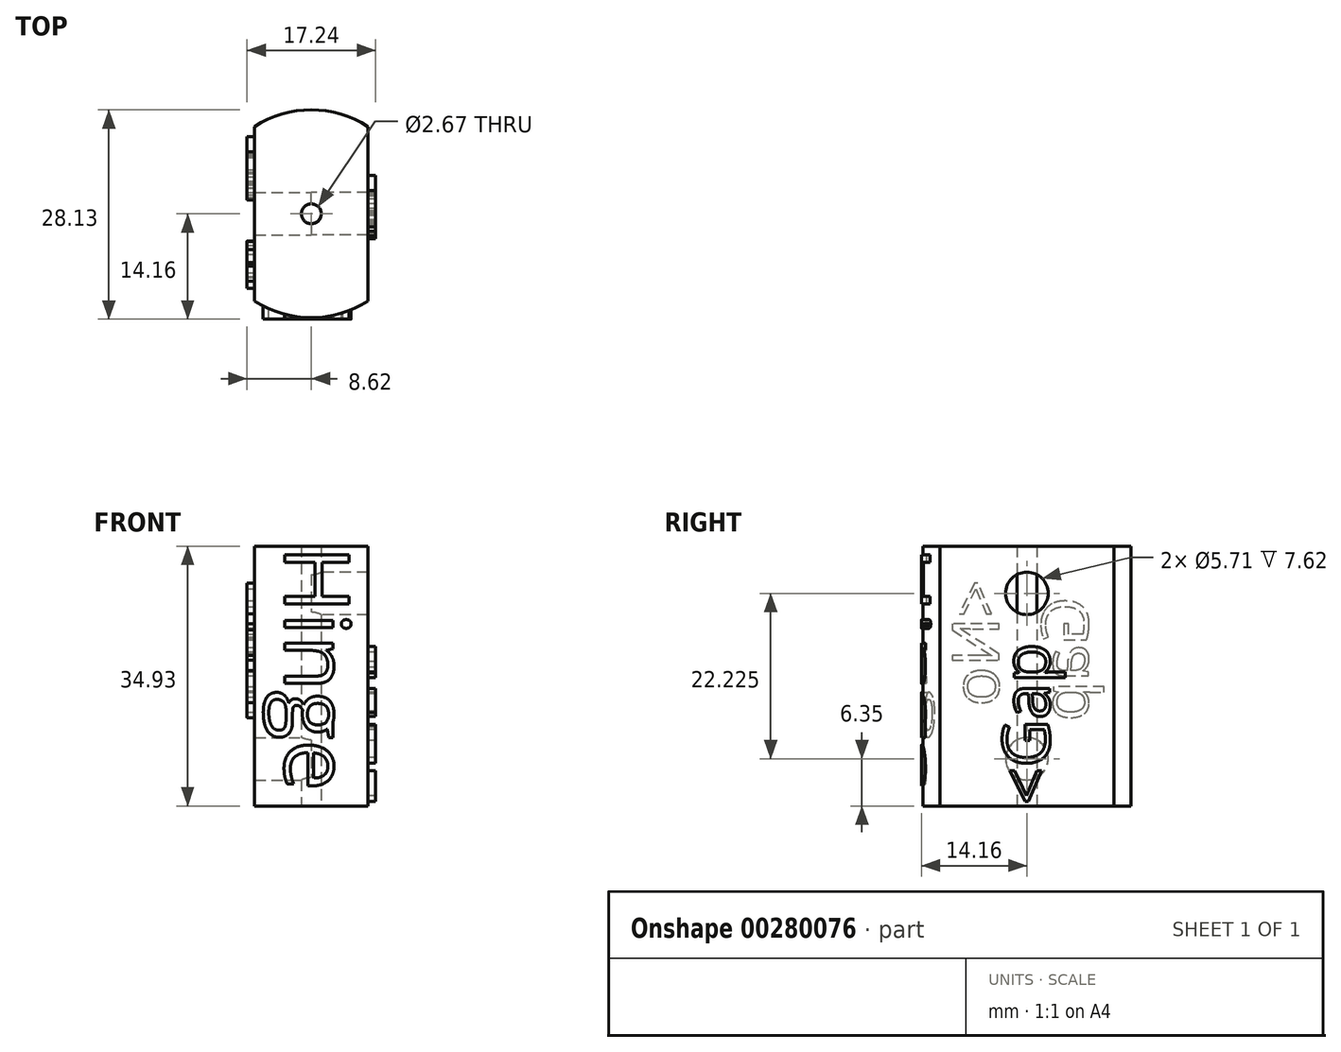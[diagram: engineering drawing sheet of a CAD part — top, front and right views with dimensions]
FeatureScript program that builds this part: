
annotation { "Feature Type Name" : "Feature", "Feature Type Description" : "" }
export const myFeature = defineFeature(function(context is Context, id is Id, definition is map)
    precondition{}
    {
        {
            var Q0;
            Q0=qCreatedBy(makeId("Top.planeOp"),FACE);
            var sketch = newSketch(context, id + "F0", { "sketchPlane" : qUnion([Q0])});
            skArc(sketch, "E0", {"start": v(-7.62, -11.7) * mm, "mid": v(0, -13.97) * mm, "end": v(7.62, -11.7) * mm});
            skCircle(sketch, "E1", {"center": v(0, 0) * mm, "radius": 1.33 * mm});
            skLineSegment(sketch, "E2", {"start": v(-7.62, -11.7) * mm, "end": v(-7.62, 11.7) * mm});
            skLineSegment(sketch, "E3.MirrorCS", {"start": v(7.62, -11.7) * mm, "end": v(7.62, 11.7) * mm});
            skArc(sketch, "E4.trimOffspring", {"start": v(7.62, 11.7) * mm, "mid": v(0, 13.97) * mm, "end": v(-7.62, 11.7) * mm});
            skSolve(sketch);
        }
        {
            var Q0;
            Q0=qSketchRegion(id+"F0",true);
            extrude(context, id + "F1", {"entities" : qUnion([Q0]), "depth" : 34.92 * mm});
        }
        {
            var Q0;
            Q0=qCreatedBy(makeId("Right.planeOp"),FACE);
            var sketch = newSketch(context, id + "F2", { "sketchPlane" : qUnion([Q0])});
            skCircle(sketch, "E5", {"center": v(0, 28.58) * mm, "radius": 2.86 * mm});
            skSolve(sketch);
        }
        {
            var Q0;
            Q0=qSketchRegion(id+"F2",true);
            var Q1;
            Q1=makeQuery(id+"F1.opExtrude","SWEPT_FACE",FACE,{"disambiguationData":[OSD([sQuery(id+"F0.wireOp",EDGE,"E3.MirrorCS")])]});
            extrude(context, id + "F3", {"entities" : qUnion([Q0]), "operationType" : NewBodyOperationType.REMOVE, "endBound" : BoundingType.UP_TO_SURFACE, "endBoundEntityFace" : qUnion([Q1]), "depth" : 6.35 * mm});
        }
        {
            var Q0;
            Q0=qCreatedBy(makeId("Right.planeOp"),FACE);
            var sketch = newSketch(context, id + "F4", { "sketchPlane" : qUnion([Q0])});
            skCircle(sketch, "E6", {"center": v(0, 6.35) * mm, "radius": 2.86 * mm});
            skSolve(sketch);
        }
        {
            var Q0;
            Q0=qSketchRegion(id+"F4",true);
            var Q1;
            Q1=makeQuery(id+"F1.opExtrude","SWEPT_FACE",FACE,{"disambiguationData":[OSD([sQuery(id+"F0.wireOp",EDGE,"E2")])]});
            extrude(context, id + "F5", {"entities" : qUnion([Q0]), "operationType" : NewBodyOperationType.REMOVE, "endBound" : BoundingType.UP_TO_SURFACE, "oppositeDirection" : true, "endBoundEntityFace" : qUnion([Q1]), "depth" : 25.4 * mm});
        }
        {
            var Q0;
            Q0=makeQuery(id+"F1.opExtrude","SWEPT_FACE",FACE,{"disambiguationData":[OSD([sQuery(id+"F0.wireOp",EDGE,"E2")])]});
            var sketch = newSketch(context, id + "F6", { "sketchPlane" : qUnion([Q0])});
            skText(sketch, "E7", { "text": " <No\n  Gap", "fontName": "OpenSans-Regular.ttf"});
            const initialGuessF6  = {"E7": [0.00374, 0.03269, 0, -1, 0.00635]};
            skSetInitialGuess(sketch, initialGuessF6);
            skSolve(sketch);
        }
        {
            var Q0;
            Q0=qSketchRegion(id+"F6",true);
            extrude(context, id + "F7", {"entities" : qUnion([Q0]), "operationType" : NewBodyOperationType.ADD, "depth" : 1 * mm});
        }
        {
            var Q0;
            Q0=makeQuery(id+"F1.opExtrude","SWEPT_FACE",FACE,{"disambiguationData":[OSD([sQuery(id+"F0.wireOp",EDGE,"E3.MirrorCS")])]});
            var sketch = newSketch(context, id + "F8", { "sketchPlane" : qUnion([Q0])});
            skText(sketch, "E8", { "text": "<Gap", "fontName": "OpenSans-Regular.ttf"});
            const initialGuessF8  = {"E8": [0.00304, 0.00015, 0, 1, 0.00635]};
            skSetInitialGuess(sketch, initialGuessF8);
            skSolve(sketch);
        }
        {
            var Q0;
            Q0=qSketchRegion(id+"F8",true);
            extrude(context, id + "F9", {"entities" : qUnion([Q0]), "operationType" : NewBodyOperationType.ADD, "depth" : 1 * mm});
        }
        {
            var Q0;
            Q0=qCreatedBy(makeId("Front.planeOp"),FACE);
            cPlane(context, id + "F10", {"entities" : qUnion([Q0]), "cplaneType" : CPlaneType.OFFSET, "offset" : 10.16 * mm, "width" : 152.4 * mm, "height" : 152.4 * mm});
        }
        {
            var Q0;
            Q0=qCreatedBy(id+"F10.planeOp",FACE);
            var sketch = newSketch(context, id + "F11", { "sketchPlane" : qUnion([Q0])});
            skText(sketch, "E9", { "text": "Hinge", "fontName": "OpenSans-Regular.ttf"});
            const initialGuessF11  = {"E9": [-0.00355, 0.03493, 0, -1, 0.00872]};
            skSetInitialGuess(sketch, initialGuessF11);
            skSolve(sketch);
        }
        {
            var Q0;
            Q0 = qSketchRegion(id + "F11", true);
            extrude(context, id + "F12", {"entities" : qUnion([Q0]), "operationType" : NewBodyOperationType.ADD, "depth" : 4 * mm});
        }
    });
